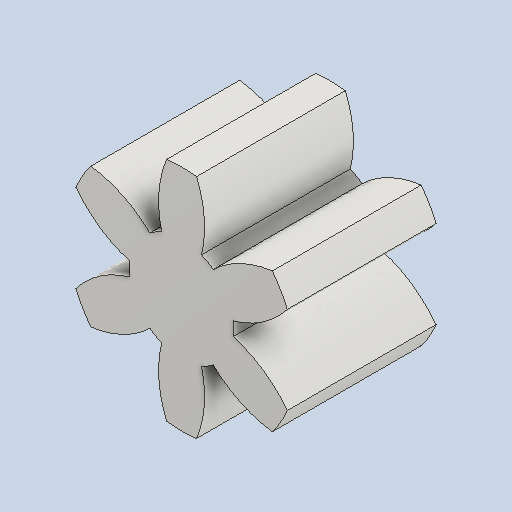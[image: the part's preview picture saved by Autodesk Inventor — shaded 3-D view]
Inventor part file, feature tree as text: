
AUTODESK INVENTOR PART (.ipt)
format: ipt  version: 2023.1 (Build 271208000, 208)  size: 183,296 bytes
history: native  units: mm (DEFAULTED — no unit token found)
features: plane x3, other x3, sketch x2, extrude x1
ambient origin geometry x8: Origin, YZ Plane, XZ Plane, XY Plane, X Axis, Y Axis, Z Axis, Center Point
bodies: Solid1 (feature_tree)
feature tree (9):
  extrude  "Extrusion1"  Depth=10.0mm TaperAngle=0.0deg
  plane  "Work Plane2"
  plane  "Work Plane8"
  plane  "Work Plane9"
  other  "Spur Gear"
  sketch  "Sketch1"  dims[d0=15.376043mm d1=10.0mm d2=0.0mm]
  sketch  "Sketch2"  dims[d3=12.0mm d4=10.0mm d5=0.0mm d16=20.0mm d17=0.0mm d34=30.0deg d39=0.0mm d41=0.0mm d43=20.0mm d46=20.0mm d47=0.0mm d48=0.0mm]
  other  "Srf1"
  other  "Pitch Diameter"
